# Revit family: IS_LDV_E2676_BIM_GB
name_source: partatom
category: Plumbing Fixtures
units: mm (PartAtom-declared; Revit-internal decimal feet)

## family parameters
Cut with Voids When Loaded = No
Host = Face
Maintain Annotation Orientation = No
OmniClass Number = 23.45.05.14.14
OmniClass Title = Sinks/Lavatories
Part Type = Normal
Room Calculation Point = No
Round Connector Dimension = Use Diameter
Shared = Yes

## types (2) — shared parameters
Accessories = https://www.idealstandard.co.uk
AreaUnits = millimeters
Assembly Code = C1030200
AssetType = Fixed
BIMObjectName = IS_LDV_Basin_E2676
Brand = Ideal Standard
Color = White
ConnectionType = Plumbing
Default Elevation = 850 mm  [stored 2.78871 ft]
DrainSize = 46 mm  [stored 0.150919 ft]
DurationUnit = year
ECA = No
EPD = https://www.idealstandard.co.uk
ExpectedLife = 30
Help = https://www.idealstandard.co.uk
IfcExportAs = IfcSanitaryType
IfcExportType = WASHHANDBASIN
InstallationInstructions = https://www.idealstandard.co.uk
LinearUnits = millimeters
Manufacturer = Ideal Standard
ManufacturerURL = https://www.idealstandard.co.uk
Material = Fine Fireclay
NBSDescription = Sinks
NBSReference = Pr_40_20_96_81
Name = Basin_LDV_E2676_IdealStandard
NettWeight = 23
NominalDepth = 472 mm
NominalHeight = 144 mm
NominalLength = 472 mm
NominalWidth = 860 mm
ProductInformation = https://www.idealstandard.co.uk
Shape = Sculptured
Size = 860 x 472 x 144 mm
Space = Internal
URL = https://www.idealstandard.co.uk
Uniclass2015Code = Pr_40_20_96_81
Uniclass2015Description = Sinks
Uniclass2015Title = Sinks
Uniclass2015Version = Products v1.33
Version = 1
VolumeUnits = Litres
WRAS = No
WarrantyDescription = Manufacturers Warranty
WarrantyDurationParts = 99
WarrantyDurationUnit = year
WarrantyGuarantorParts = Ideal Standard
WashHandBasinMounting = Wall mounted
WashHandBasinType = Hand Rinse
WaterEfficientProduct = No
zero-valued in all types: CWFU, Cost, HWFU, WFU

## per-type parameters (varying)
| type | BarCode | Description | Features | Finish | Model | ModelNumber | ModelReference |
| E267601 - LDV VTY 86 3TH WHITE BXD | 5017830563976 | La Dolce Vita® vanity basin 86 cm with 3 taphole, with slotted overflow, white | La Dolce Vita® vanity basin 86 cm with 3 taphole, with slotted overflow, white, in carton box, EU pallet | white | E267601 | E267601 | La Dolce Vita® vanity basin 86 cm with 3 taphole, with slotted overflow, white |
| E2676MA - LDV VTY 86 3TH WHITE IP BXD | 5017830563983 | La Dolce Vita® vanity basin 86 cm with 3 taphole, with slotted overflow, white Ideal Plus | La Dolce Vita® vanity basin 86 cm with 3 taphole, with slotted overflow, white Ideal Plus, in carton box, EU pallet | white Ideal Plus | E2676MA | E2676MA | La Dolce Vita® vanity basin 86 cm with 3 taphole, with slotted overflow, white Ideal Plus |

note: [stored X ft] marks values corroborated as IEEE doubles in the binary element streams (Revit-internal decimal feet)

## geometry (parser evidence)
native form markers: Sweep x3
no freeform markers — native parametric forms only
